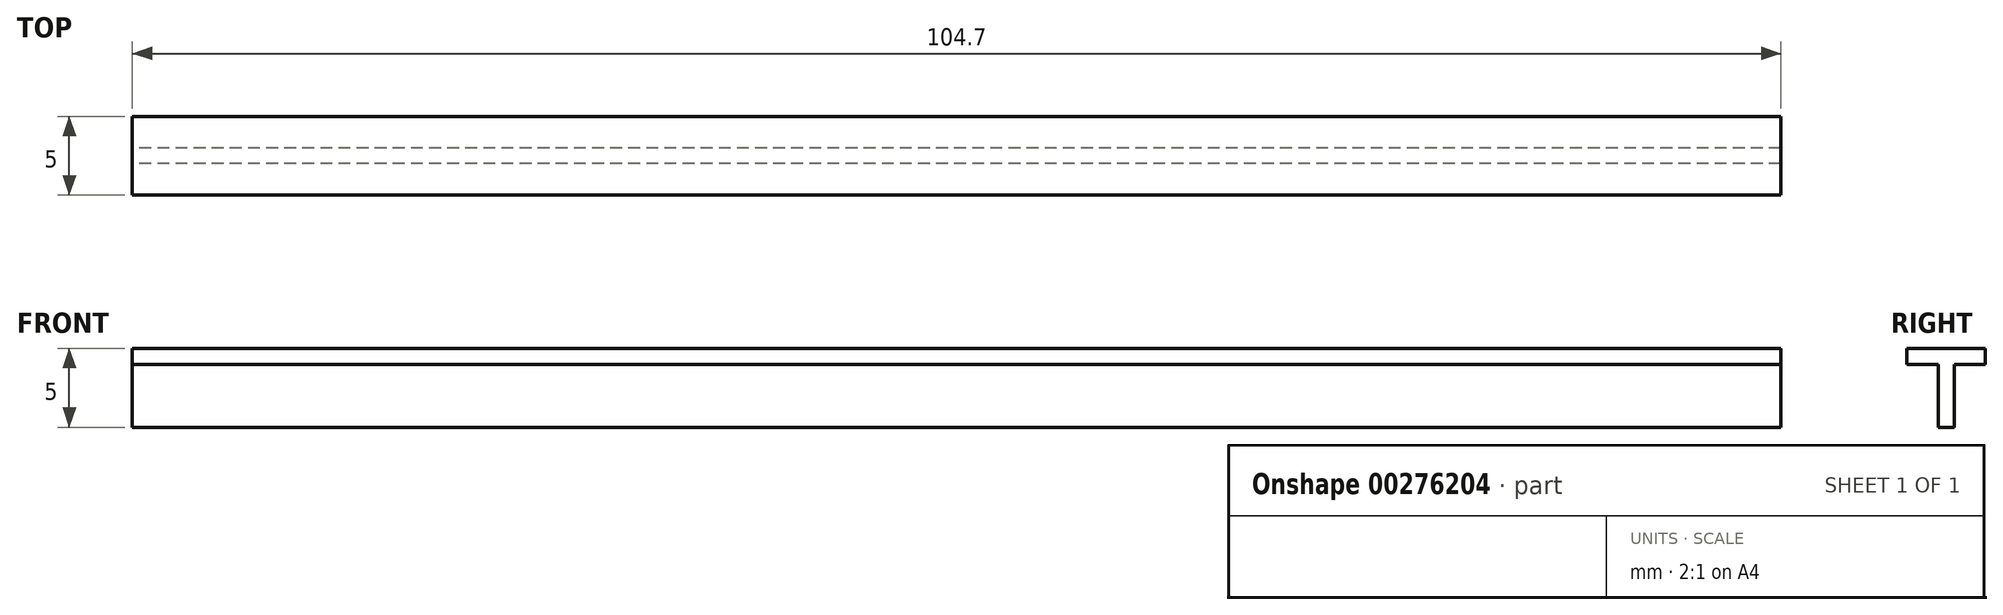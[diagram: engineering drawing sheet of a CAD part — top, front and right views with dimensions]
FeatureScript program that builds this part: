
annotation { "Feature Type Name" : "Feature", "Feature Type Description" : "" }
export const myFeature = defineFeature(function(context is Context, id is Id, definition is map)
    precondition{}
    {
        {
            var Q0;
            Q0=qCreatedBy(makeId("Right.planeOp"),FACE);
            var sketch = newSketch(context, id + "F0", { "sketchPlane" : qUnion([Q0]), "asVersion" : FeatureScriptVersionNumber.V660_ENCLOSE_AUTO_MATCHING, "asVersion" : FeatureScriptVersionNumber.V660_ENCLOSE_AUTO_MATCHING});
            skLineSegment(sketch, "E0", {"start": v(2.5, 0) * mm, "end": v(2.5, -1) * mm});
            skLineSegment(sketch, "E1", {"start": v(2.5, -1) * mm, "end": v(0.5, -1) * mm});
            skLineSegment(sketch, "E2", {"start": v(0.5, -1) * mm, "end": v(0.5, -5) * mm});
            skLineSegment(sketch, "E3", {"start": v(2.5, 0) * mm, "end": v(0, 0) * mm});
            skLineSegment(sketch, "E4", {"start": v(0.5, -5) * mm, "end": v(0, -5) * mm});
            skLineSegment(sketch, "E5", {"start": v(0, -16.51) * mm, "end": v(0, 5.46) * mm, "construction": true});
            skLineSegment(sketch, "E6.MirrorCS", {"start": v(-2.5, 0) * mm, "end": v(-2.5, -1) * mm});
            skLineSegment(sketch, "E7.MirrorCS", {"start": v(-0.5, -5) * mm, "end": v(0, -5) * mm});
            skLineSegment(sketch, "E8.MirrorCS", {"start": v(-2.5, 0) * mm, "end": v(0, 0) * mm});
            skLineSegment(sketch, "E9.MirrorCS", {"start": v(-0.5, -1) * mm, "end": v(-0.5, -5) * mm});
            skLineSegment(sketch, "E10.MirrorCS", {"start": v(-2.5, -1) * mm, "end": v(-0.5, -1) * mm});
            skSolve(sketch);
        }
        {
            var Q0;
            Q0=makeQuery(id+"F0.imprint","IMPRINT",FACE,{"disambiguationData":[TD([[makeQuery(id+"F0.imprint","IMPRINT",EDGE,{"derivedFrom":sQuery(id+"F0.wireOp",EDGE,"E0")}),-1.0]])]});
            extrude(context, id + "F1", {"entities" : qUnion([Q0]), "depth" : 104.7 * mm, "offsetDistance" : 25 * mm, "symmetric" : true});
        }
    });
